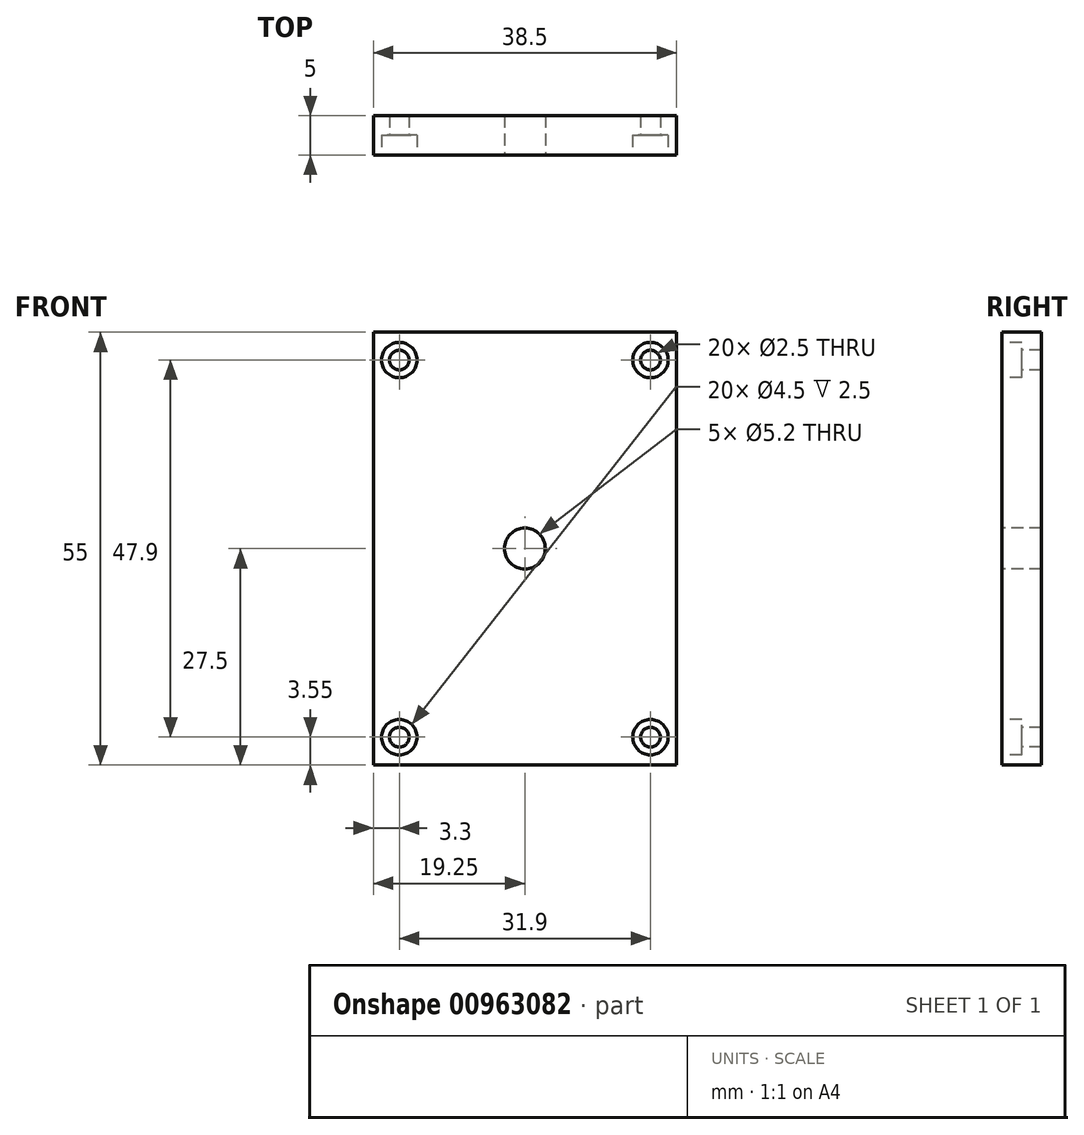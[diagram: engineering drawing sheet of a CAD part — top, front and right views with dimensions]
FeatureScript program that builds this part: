
annotation { "Feature Type Name" : "Feature", "Feature Type Description" : "" }
export const myFeature = defineFeature(function(context is Context, id is Id, definition is map)
    precondition{}
    {
        {
            var Q0;
            Q0=qCreatedBy(makeId("Front.planeOp"),FACE);
            var sketch = newSketch(context, id + "F0", { "sketchPlane" : qUnion([Q0])});
            skLineSegment(sketch, "E0.bottom", {"start": v(0, 0) * mm, "end": v(38.5, 0) * mm});
            skLineSegment(sketch, "E0.top", {"start": v(0, 55) * mm, "end": v(38.5, 55) * mm});
            skLineSegment(sketch, "E0.left", {"start": v(0, 0) * mm, "end": v(0, 55) * mm});
            skLineSegment(sketch, "E0.right", {"start": v(38.5, 0) * mm, "end": v(38.5, 55) * mm});
            skLineSegment(sketch, "E1", {"start": v(0, 27.5) * mm, "end": v(38.5, 27.5) * mm, "construction": true});
            skLineSegment(sketch, "E2", {"start": v(19.25, 55) * mm, "end": v(19.25, 0) * mm, "construction": true});
            skCircle(sketch, "E3", {"center": v(19.25, 27.5) * mm, "radius": 2.6 * mm});
            skPoint(sketch, "E4", {"position": v(3.3, 3.55) * mm});
            skPoint(sketch, "E5.MirrorP", {"position": v(35.2, 3.55) * mm});
            skLineSegment(sketch, "E6.MirrorCS", {"start": v(38.5, 27.5) * mm, "end": v(0, 27.5) * mm, "construction": true});
            skPoint(sketch, "E7.MirrorP", {"position": v(3.3, 51.45) * mm});
            skPoint(sketch, "E8.MirrorP", {"position": v(35.2, 51.45) * mm});
            skSolve(sketch);
        }
        {
            var Q0;
            Q0=makeQuery(id+"F0.imprint","IMPRINT",FACE,{"disambiguationData":[TD([[makeQuery(id+"F0.imprint","IMPRINT",EDGE,{"derivedFrom":sQuery(id+"F0.wireOp",EDGE,"E0.bottom")}),1.0]])]});
            extrude(context, id + "F1", {"entities" : qUnion([Q0]), "oppositeDirection" : true, "depth" : 5 * mm, "offsetDistance" : 25 * mm});
        }
        {
            var Q0;
            Q0=sQuery(id+"F0.wireOp",VERTEX,"E4");
            var Q1;
            Q1=sQuery(id+"F0.wireOp",VERTEX,"E5.MirrorP");
            var Q2;
            Q2=sQuery(id+"F0.wireOp",VERTEX,"E8.MirrorP");
            var Q3;
            Q3=sQuery(id+"F0.wireOp",VERTEX,"E7.MirrorP");
            var Q4;
            Q4=makeQuery(id+"F1.opExtrude","SWEPT_BODY",BODY,{"disambiguationData":[OSD([sQuery(id+"F0.wireOp",EDGE,"E0.bottom"),sQuery(id+"F0.wireOp",EDGE,"E0.top"),sQuery(id+"F0.wireOp",EDGE,"E0.left"),sQuery(id+"F0.wireOp",EDGE,"E0.right"),sQuery(id+"F0.wireOp",EDGE,"E3")])]});
            hole(context, id + "F2", {"style" : HoleStyle.C_BORE, "endStyle" : HoleEndStyle.THROUGH, "holeDiameter" : 2.5 * mm, "cBoreDiameter" : 4.5 * mm, "cBoreDepth" : 2.5 * mm, "majorDiameter" : 5 * mm, "isTappedThrough" : true, "tappedDepth" : 12 * mm, "tapClearance" : 3, "locations" : qUnion([Q0, Q1, Q2, Q3]), "scope" : qUnion([Q4])});
        }
    });
